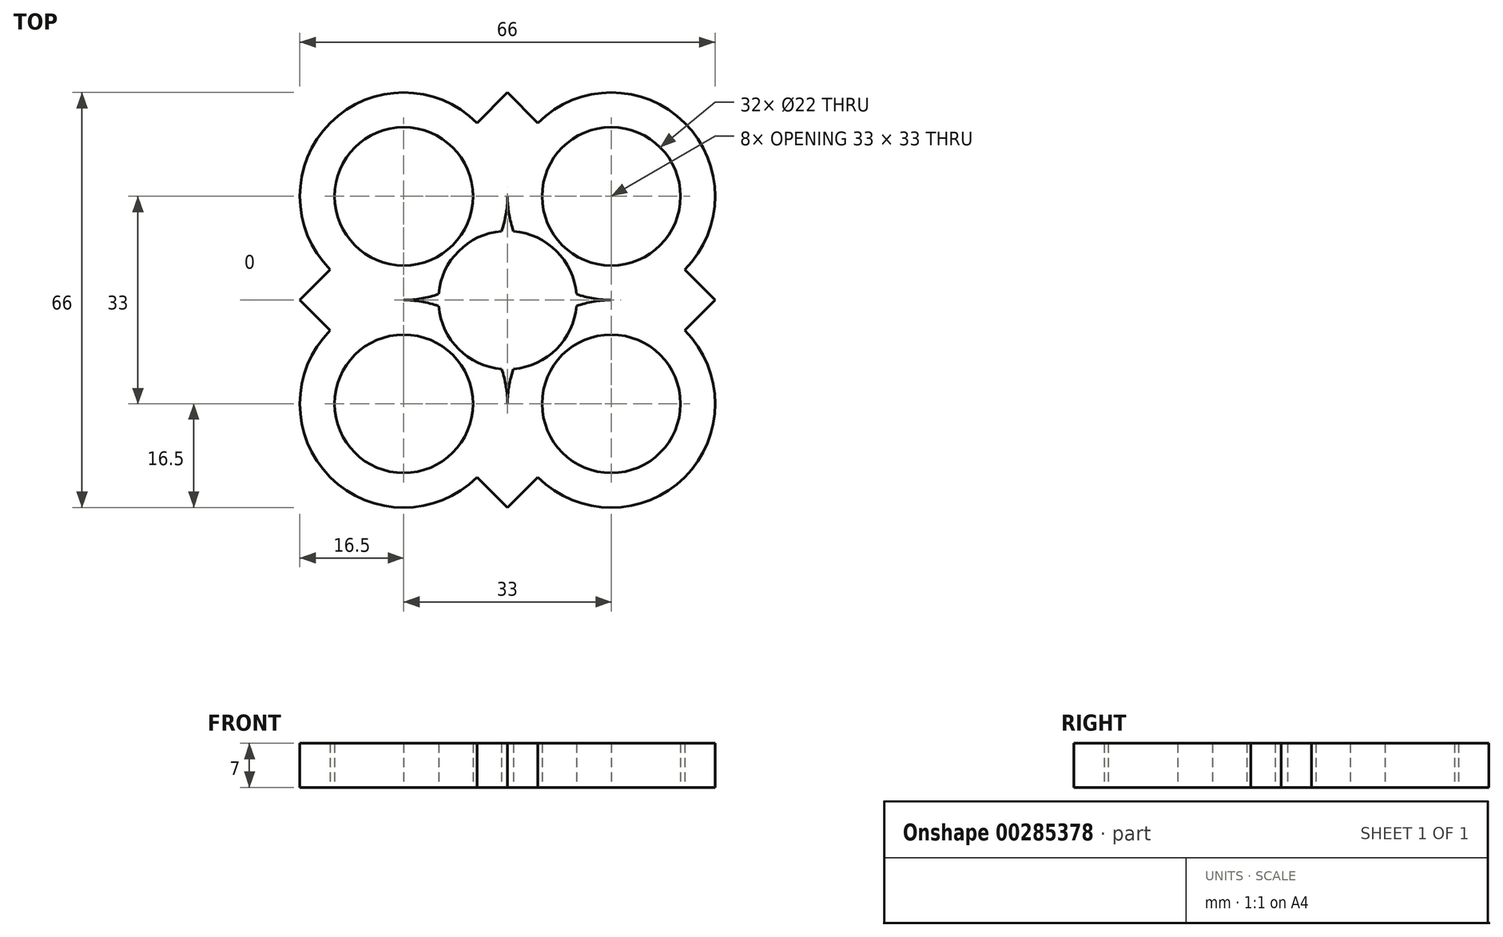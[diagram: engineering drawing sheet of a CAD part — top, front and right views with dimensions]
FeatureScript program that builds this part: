
annotation { "Feature Type Name" : "Feature", "Feature Type Description" : "" }
export const myFeature = defineFeature(function(context is Context, id is Id, definition is map)
    precondition{}
    {
        {
            var Q0;
            Q0=qCreatedBy(makeId("Top.planeOp"),FACE);
            var sketch = newSketch(context, id + "F0", { "sketchPlane" : qUnion([Q0])});
            skCircle(sketch, "E0", {"center": v(0, 0) * mm, "radius": 11 * mm});
            skLineSegment(sketch, "E1", {"start": v(33, 33) * mm, "end": v(-16.5, -16.5) * mm});
            skLineSegment(sketch, "E2", {"start": v(-33, 0) * mm, "end": v(0, 0) * mm});
            skLineSegment(sketch, "E3", {"start": v(0, 0) * mm, "end": v(33, 0) * mm});
            skLineSegment(sketch, "E4", {"start": v(33, 0) * mm, "end": v(0, 33) * mm});
            skLineSegment(sketch, "E5", {"start": v(0, 33) * mm, "end": v(-33, 0) * mm});
            skLineSegment(sketch, "E6", {"start": v(0, -33) * mm, "end": v(-33, 0) * mm});
            skLineSegment(sketch, "E7", {"start": v(0, -33) * mm, "end": v(33, 0) * mm});
            skCircle(sketch, "E8", {"center": v(-16.5, 16.5) * mm, "radius": 11 * mm});
            skCircle(sketch, "E9", {"center": v(-16.5, -16.5) * mm, "radius": 11 * mm});
            skCircle(sketch, "E10", {"center": v(16.5, 16.5) * mm, "radius": 11 * mm});
            skCircle(sketch, "E11", {"center": v(16.5, -16.5) * mm, "radius": 11 * mm});
            skCircle(sketch, "E12", {"center": v(-16.5, 16.5) * mm, "radius": 16.5 * mm});
            skCircle(sketch, "E13", {"center": v(16.5, 16.5) * mm, "radius": 16.5 * mm});
            skCircle(sketch, "E14", {"center": v(16.5, -16.5) * mm, "radius": 16.5 * mm});
            skCircle(sketch, "E15", {"center": v(-16.5, -16.5) * mm, "radius": 16.5 * mm});
            skLineSegment(sketch, "E16.trimOffspring", {"start": v(-16.5, 16.5) * mm, "end": v(16.5, -16.5) * mm});
            skPoint(sketch, "E17.start.orphan", {"position": v(-33, 33) * mm});
            skPoint(sketch, "E18.orphan", {"position": v(-33, -33) * mm});
            skPoint(sketch, "E19.trimOffspring.end.orphan", {"position": v(33, -33) * mm});
            skSolve(sketch);
        }
        {
            var Q0;
            Q0 = qSketchRegion(id + "F0", true);
            extrude(context, id + "F1", {"entities" : qUnion([Q0]), "depth" : 7 * mm});
        }
    });
